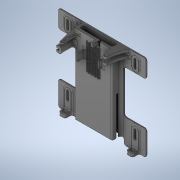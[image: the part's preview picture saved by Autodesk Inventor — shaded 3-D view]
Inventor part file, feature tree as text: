
AUTODESK INVENTOR PART (.ipt)
format: ipt  version: 2020 (Build 240168000, 168)  size: 2,559,488 bytes
history: native  units: mm
features: fillet x35, sketch x29, projected_geometry x29, extrude x28, plane x8, hole x3, pattern_linear x3, mirror x1
ambient origin geometry x8: Origin, YZ Plane, XZ Plane, XY Plane, X Axis, Y Axis, Z Axis, Center Point
bodies: Solid1 (feature_tree)
feature tree (136):
  extrude  "Extrusion1"  Depth=175.0mm
  plane  "Work Plane1"
  extrude  "Extrusion2"  [1 undecoded]
  extrude  "Extrusion3"  Depth=17.0mm
  extrude  "Extrusion4"  Depth=4.5mm
  extrude  "Extrusion24"  Depth=8.0mm TaperAngle=0.0deg
  sketch  "Sketch5"  dims[d12=85.0mm d13=8.0mm d14=0.0mm]
  extrude  "Extrusion5"  Depth=55.0mm
  extrude  "Extrusion6"  Depth=8.0mm TaperAngle=0.0deg
  extrude  "Extrusion7"  Depth=3.0mm
  extrude  "Extrusion8"  Depth=37.5mm
  extrude  "Extrusion9"  Depth=8.0mm TaperAngle=0.0deg
  extrude  "Extrusion10"  Depth=11.0mm
  extrude  "Extrusion11"  Depth=6.0mm TaperAngle=0.0deg
  hole  "Hole1"  [1 undecoded]
  extrude  "Extrusion12"  TaperAngle=0.0deg  [1 undecoded]
  plane  "Work Plane2"
  plane  "Work Plane3"
  sketch  "Sketch13"  dims[d33=3.0mm d34=11.0mm]
  plane  "Work Plane4"
  extrude  "Extrusion13"  Depth=6.0mm
  extrude  "Extrusion14"  Depth=10.5mm TaperAngle=0.0deg
  sketch  "Sketch15"  dims[d38=27.5mm d39=6.0mm]
  plane  "Work Plane5"
  extrude  "Extrusion15"  Depth=10.0mm
  extrude  "Extrusion16"  Depth=3.0mm
  extrude  "Extrusion17"  Depth=16.0mm TaperAngle=0.0deg
  extrude  "Extrusion20"  Depth=0.5mm
  plane  "Work Plane6"
  mirror  "Mirror1"
  hole  "Hole4"  [1 undecoded]
  extrude  "Extrusion22"  Depth=30.0mm
  plane  "Work Plane7"
  extrude  "Extrusion23"  Depth=10.0mm TaperAngle=0.0deg
  extrude  "Extrusion30"  Depth=10.0mm TaperAngle=0.0deg
  extrude  "Extrusion31"  Depth=10.0mm TaperAngle=0.0deg
  hole  "Hole6"  [1 undecoded]
  extrude  "Extrusion32"  Depth=2.5mm TaperAngle=0.0deg
  fillet  "Fillet38"  Radius=3.0mm
  fillet  "Fillet39"  Radius=60.0mm
  fillet  "Fillet4"  Radius=3.0mm
  fillet  "Fillet44"  Radius=3.25mm
  fillet  "Fillet41"  Radius=10.0mm
  extrude  "Extrusion33"  Depth=0.5mm
  plane  "Work Plane13"
  extrude  "Extrusion34"  Depth=0.5mm
  fillet  "Fillet5"  Radius=50.0mm
  fillet  "Fillet6"  Radius=10.0mm
  fillet  "Fillet7"  Radius=0.5mm
  fillet  "Fillet8"  Radius=40.0mm
  fillet  "Fillet9"  Radius=150.0mm
  fillet  "Fillet10"  Radius=34.5mm
  fillet  "Fillet11"  [1 undecoded]
  fillet  "Fillet12"  Radius=4.0mm
  fillet  "Fillet13"  Radius=18.5mm
  fillet  "Fillet14"  Radius=75.0mm
  fillet  "Fillet15"  Radius=6.0mm
  fillet  "Fillet16"  Radius=3.1mm
  fillet  "Fillet17"  Radius=8.0mm
  fillet  "Fillet20"  Radius=5.75mm
  fillet  "Fillet24"  Radius=2.5mm
  fillet  "Fillet21"  [1 undecoded]
  fillet  "Fillet22"  Radius=83.0mm
  fillet  "Fillet36"  Radius=3.2mm
  fillet  "Fillet23"  Radius=3.490659mm
  fillet  "Fillet18"  Radius=79.0mm
  fillet  "Fillet28"  Radius=3.0mm
  fillet  "Fillet29"  Radius=5.0mm
  fillet  "Fillet30"  Radius=3.0mm
  fillet  "Fillet31"  Radius=3.0mm
  sketch  "Sketch18"  dims[d45=16.0mm d46=0.0mm d47=3.0mm]
  extrude  "Extrusion18"  Depth=0.5mm
  fillet  "Fillet1"  Radius=3.0mm
  pattern_linear  "Rectangular Pattern2"  Spacing1=0.5mm  [1 undecoded]
  extrude  "Extrusion19"  Depth=0.5mm
  fillet  "Fillet2"  Radius=1.0mm
  pattern_linear  "Rectangular Pattern3"  Spacing1=1.0mm  [1 undecoded]
  pattern_linear  "Rectangular Pattern4"  Spacing1=1.0mm  [1 undecoded]
  fillet  "Fillet33"  Radius=2.0mm
  fillet  "Fillet34"  Radius=2.0mm
  fillet  "Fillet35"  Radius=1.0mm
  fillet  "Fillet37"  Radius=1.0mm
  sketch  "Sketch1"  dims[d0=84.0mm d1=175.0mm]
  sketch  "Sketch2"  dims[d2=11.0mm d3=11.0mm d4=0.0mm d5=0.0mm d6=-2.5mm]
  sketch  "Sketch3"  dims[d7=79.0mm d8=17.0mm]
  projected_geometry  "Projected Loop1"
  sketch  "Sketch4"  dims[d9=8.0mm d10=0.0mm d11=4.5mm]
  projected_geometry  "Projected Loop2"
  projected_geometry  "Projected Loop3"
  sketch  "Sketch6"  dims[d15=6.0mm d16=55.0mm]
  projected_geometry  "Projected Loop4"
  sketch  "Sketch7"  dims[d17=40.0mm d18=8.0mm d19=0.0mm]
  projected_geometry  "Projected Loop5"
  sketch  "Sketch8"  dims[d20=37.5mm d21=3.0mm]
  projected_geometry  "Projected Loop6"
  sketch  "Sketch9"  dims[d22=16.0mm d23=37.5mm]
  projected_geometry  "Projected Loop7"
  sketch  "Sketch10"  dims[d24=18.5mm d25=0.0mm d26=8.0mm d27=0.0mm]
  projected_geometry  "Projected Loop8"
  sketch  "Sketch11"  dims[d28=3.0mm d29=11.0mm]
  projected_geometry  "Projected Loop9"
  sketch  "Sketch12"  dims[d30=2.5mm d31=6.0mm d32=0.0mm]
  projected_geometry  "Projected Loop10"
  projected_geometry  "Projected Loop11"
  sketch  "Sketch14"  dims[d35=2.5mm d36=0.0mm d37=0.0mm]
  projected_geometry  "Projected Loop12"
  projected_geometry  "Projected Loop13"
  sketch  "Sketch16"  dims[d40=8.0mm d41=10.5mm d42=0.0mm]
  projected_geometry  "Projected Loop14"
  sketch  "Sketch17"  dims[d43=4.0mm d44=10.0mm]
  projected_geometry  "Projected Loop15"
  projected_geometry  "Projected Loop16"
  sketch  "Sketch19"  dims[d48=1.0mm d49=16.0mm d50=0.0mm]
  projected_geometry  "Projected Loop17"
  sketch  "Sketch22"  dims[d51=4.0mm]
  sketch  "Sketch23"  dims[d52=3.2mm d53=6.0mm d54=4.0mm d55=2.0mm d56=90.0deg d57=0.5mm d58=0.0mm d59=5.75mm]
  sketch  "Sketch24"  dims[d60=2.0mm d61=0.0mm d62=15.0mm]
  sketch  "Sketch26"  dims[d63=10.0mm d64=30.0mm]
  sketch  "Sketch33"  dims[d65=30.0mm d66=10.0mm d67=0.0mm]
  projected_geometry  "Projected Loop28"
  projected_geometry  "Projected Loop29"
  sketch  "Sketch34"  dims[d68=30.0deg d69=10.0mm d70=0.0mm]
  projected_geometry  "Projected Loop30"
  projected_geometry  "Projected Loop31"
  sketch  "Sketch35"  dims[d72=-4.0mm d73=10.0mm d74=0.0mm]
  projected_geometry  "Projected Loop32"
  projected_geometry  "Projected Loop33"
  sketch  "Sketch36"  dims[d75=3.2mm d76=10.0mm d77=0.0mm]
  sketch  "Sketch37"  dims[d78=5.75mm d79=2.5mm d80=0.0mm d81=3.0mm d82=60.0mm d83=3.0mm d84=3.25mm d85=10.0mm d86=0.0mm]
  projected_geometry  "Projected Loop34"
  projected_geometry  "Projected Loop35"
  projected_geometry  "Projected Loop36"
  projected_geometry  "Projected Loop37"
  sketch  "Sketch38"  dims[d87=2.0mm d88=3.5mm d89=0.5mm d96=50.0mm d98=7.0mm d99=10.0mm d100=0.0mm d101=0.5mm d102=40.0mm d104=7.0mm d105=150.0mm d107=4.0mm d109=34.5mm d111=105.0deg d112=4.0mm d113=18.5mm d114=75.0mm d115=6.0mm d116=0.0mm d117=3.1mm d118=8.0mm d129=5.75mm d130=2.5mm d131=0.0mm d132=-4.1mm d133=83.0mm d134=3.2mm d135=3.490659mm d136=79.0mm d139=3.0mm d140=0.0mm d141=5.0mm d142=3.0mm d143=3.0mm d144=4.0mm d145=3.0mm d146=0.5mm d147=2.0mm d148=1.0mm d149=1.0mm d150=1.0mm d151=2.0mm d152=2.0mm d153=1.0mm d154=1.0mm d155=3.5mm d157=0.25mm d158=1.0mm d159=2.0mm d160=2.0mm d161=5.0mm d165=0.5mm d166=0.5mm d167=2.0mm d168=0.5mm d170=0.5mm d171=2.0mm d172=0.5mm d173=5.0mm d174=5.0mm d175=0.0mm d176=0.0mm d184=2.5mm d185=4.0mm d186=0.5mm d187=3.2mm d188=6.0mm d189=4.0mm d190=2.0mm d191=90.0deg d192=8.0mm d193=20.594885mm d200=5.0mm d201=3.0mm d221=1.0mm d231=15.0mm d232=2.0mm d233=0.0mm d234=15.0mm d235=15.0mm d236=15.0mm d237=15.0mm d238=149.0mm d239=8.0mm d240=0.0mm d241=5.4mm d242=6.0mm d243=4.0mm d244=2.0mm d245=90.0deg d246=8.0mm d247=90.0deg d248=8.25mm d249=15.0mm d251=135.0mm d252=135.0mm d253=2.0mm d254=0.0mm d255=3.0mm d256=5.4mm d257=5.4mm d258=5.4mm d259=5.4mm d260=0.0mm d261=0.0mm d262=-3.5mm d263=8.25mm d264=8.25mm d265=3.5mm d266=0.0mm]
  projected_geometry  "Project Cut Edges1"
  projected_geometry  "Project Cut Edges3"
note: 10 required parameter values undecoded (feature->parameter linkage not recoverable at this tier; creation-order binding heuristic only, values carry confidence <= 0.55)
